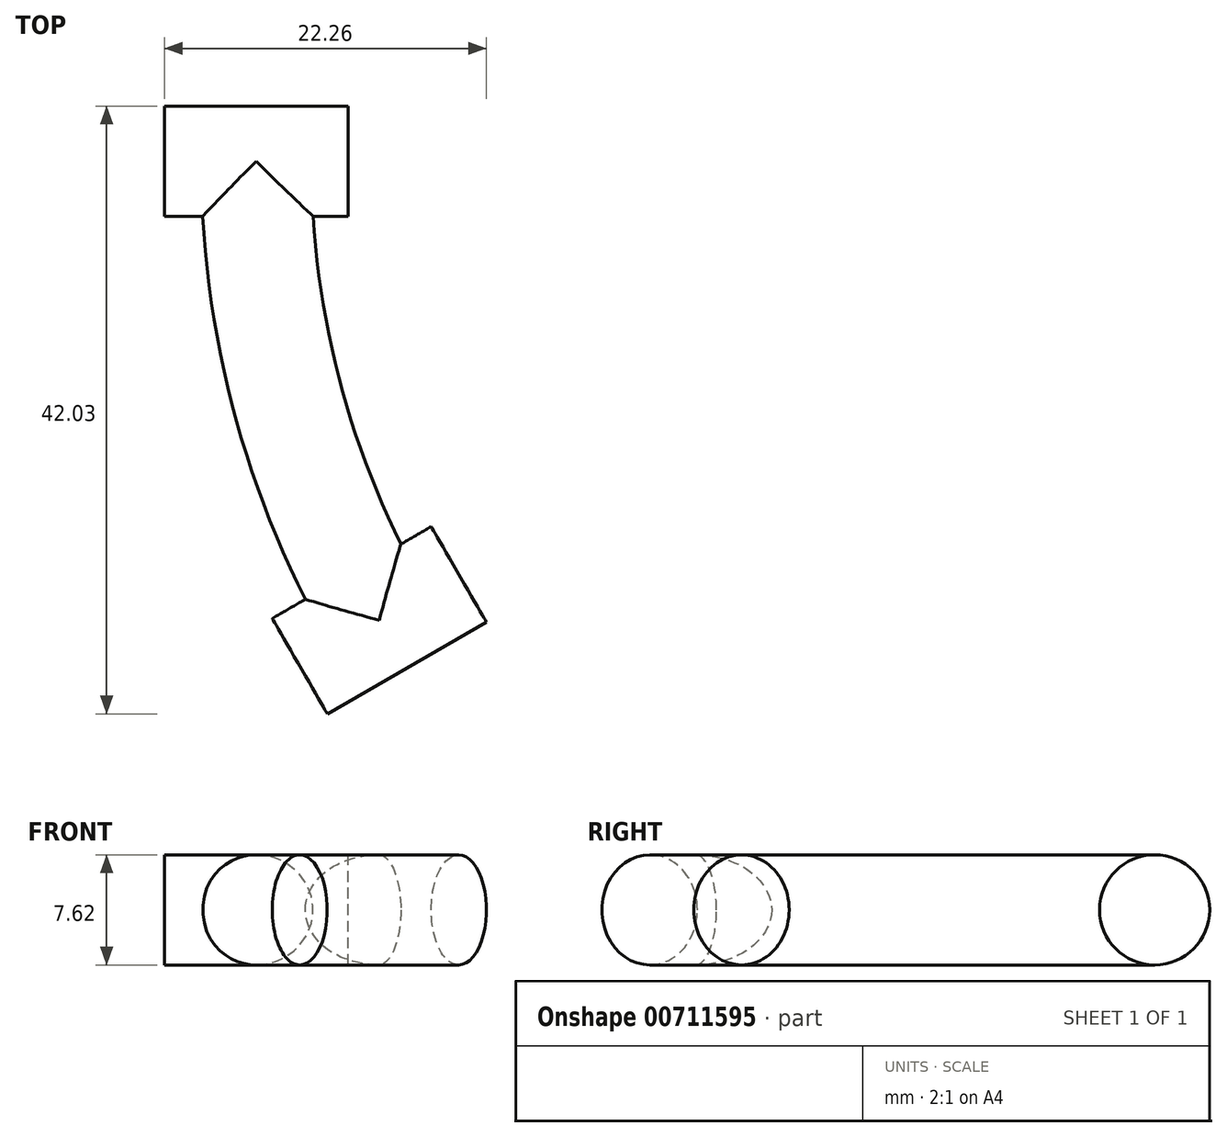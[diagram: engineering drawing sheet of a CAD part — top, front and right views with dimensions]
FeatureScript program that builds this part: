
annotation { "Feature Type Name" : "Feature", "Feature Type Description" : "" }
export const myFeature = defineFeature(function(context is Context, id is Id, definition is map)
    precondition{}
    {
        {
            var Q0;
            Q0=qCreatedBy(makeId("Front.planeOp"),FACE);
            var sketch = newSketch(context, id + "F0", { "sketchPlane" : qUnion([Q0])});
            skCircle(sketch, "E0", {"center": v(12.7, 0) * mm, "radius": 3.81 * mm});
            skSolve(sketch);
        }
        {
            var Q0;
            Q0=qCreatedBy(makeId("Top.planeOp"),FACE);
            var sketch = newSketch(context, id + "F1", { "sketchPlane" : qUnion([Q0])});
            skArc(sketch, "E1", {"start": v(0, 0) * mm, "mid": v(2.6, -19.72) * mm, "end": v(10.2, -38.1) * mm});
            skLineSegment(sketch, "E2", {"start": v(10.2, -38.1) * mm, "end": v(76.2, 0) * mm, "construction": true});
            skSolve(sketch);
        }
        {
            var Q0;
            Q0=qSketchRegion(id+"F0",true);
            var Q1;
            Q1=qConstructionFilter(qBodyType(qCreatedBy(id+"F1",EDGE),BodyType.WIRE),ConstructionObject.NO);
            sweep(context, id + "F2", {"profiles" : qUnion([Q0]), "path" : qUnion([Q1])});
        }
        {
            var Q0;
            Q0=qCreatedBy(makeId("Right.planeOp"),FACE);
            cPlane(context, id + "F3", {"entities" : qUnion([Q0]), "cplaneType" : CPlaneType.OFFSET, "offset" : 12.7 * mm, "width" : 152.4 * mm, "height" : 152.4 * mm});
        }
        {
            var Q0;
            Q0=qCreatedBy(id+"F3.planeOp",FACE);
            var sketch = newSketch(context, id + "F4", { "sketchPlane" : qUnion([Q0])});
            skCircle(sketch, "E3", {"center": v(0, 0) * mm, "radius": 3.81 * mm});
            skSolve(sketch);
        }
        {
            var Q0;
            Q0=makeQuery(id+"F4.imprint","IMPRINT",FACE,{"disambiguationData":[TD([[makeQuery(id+"F4.imprint","IMPRINT",EDGE,{"derivedFrom":sQuery(id+"F4.wireOp",EDGE,"E3")}),1.0]])]});
            var Q1;
            Q1=sQuery(id+"F4.wireOp",EDGE,"E3");
            extrude(context, id + "F5", {"entities" : qUnion([Q0]), "operationType" : NewBodyOperationType.ADD, "surfaceEntities" : qUnion([Q1]), "endBound" : BoundingType.SYMMETRIC, "depth" : 12.7 * mm, "offsetDistance" : 25.4 * mm});
        }
        {
            var Q0;
            Q0=makeQuery(id+"F2.opSweep","CAP_FACE",FACE,{"disambiguationData":[OSD([sQuery(id+"F0.wireOp",EDGE,"E0"),sQuery(id+"F1.wireOp",VERTEX,"E1.end")])],"isStart":false});
            var sketch = newSketch(context, id + "F6", { "sketchPlane" : qUnion([Q0])});
            skLineSegment(sketch, "E4", {"start": v(2.5, 3.81) * mm, "end": v(2.5, -3.81) * mm});
            skSolve(sketch);
        }
        {
            var Q0;
            Q0=sQuery(id+"F6.wireOp",EDGE,"E4");
            var Q1;
            {var subQ0=sQuery(id+"F6.wireOp",EDGE,"E4");Q1=makeQuery(id+"F6.imprint","IMPRINT",FACE,{"disambiguationData":[TD([[makeQuery(id+"F6.imprint","IMPRINT",EDGE,{"derivedFrom":subQ0}),1.0]])]});}
            cPlane(context, id + "F7", {"entities" : qUnion([Q0, Q1]), "cplaneType" : CPlaneType.LINE_ANGLE, "offset" : 25.4 * mm, "angle" : 90 * degree, "width" : 152.4 * mm, "height" : 152.4 * mm});
        }
        {
            var Q0;
            Q0=qCreatedBy(id+"F7.planeOp",FACE);
            var sketch = newSketch(context, id + "F8", { "sketchPlane" : qUnion([Q0])});
            skCircle(sketch, "E5", {"center": v(-38.1, 0) * mm, "radius": 3.8 * mm});
            skSolve(sketch);
        }
        {
            var Q0;
            Q0=makeQuery(id+"F8.imprint","IMPRINT",FACE,{"disambiguationData":[TD([[makeQuery(id+"F8.imprint","IMPRINT",EDGE,{"derivedFrom":sQuery(id+"F8.wireOp",EDGE,"E5")}),1.0]])]});
            extrude(context, id + "F9", {"entities" : qUnion([Q0]), "operationType" : NewBodyOperationType.ADD, "endBound" : BoundingType.SYMMETRIC, "depth" : 12.7 * mm, "offsetDistance" : 25.4 * mm});
        }
    });
